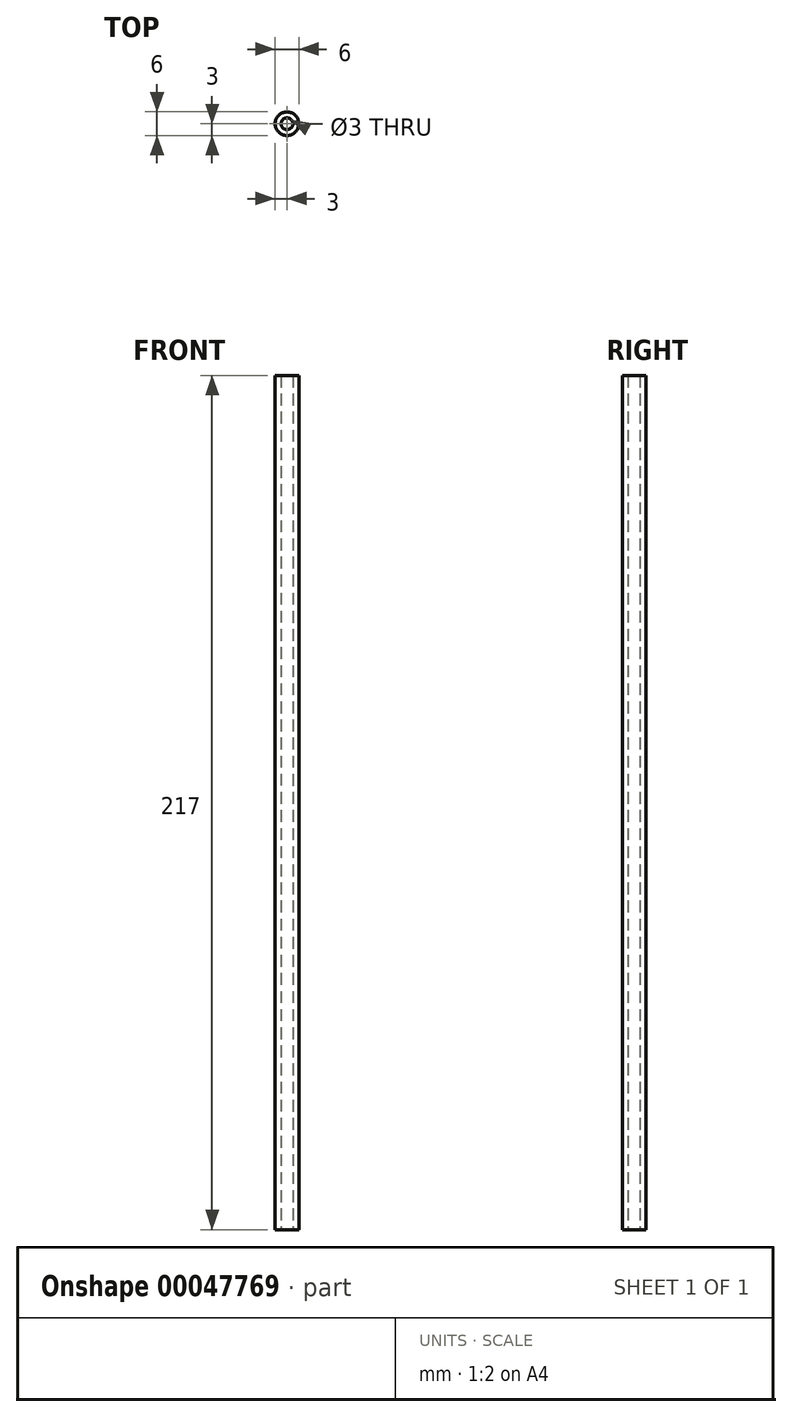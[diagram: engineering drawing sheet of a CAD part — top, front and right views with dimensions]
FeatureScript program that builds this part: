
annotation { "Feature Type Name" : "Feature", "Feature Type Description" : "" }
export const myFeature = defineFeature(function(context is Context, id is Id, definition is map)
    precondition{}
    {
        {
            var Q0;
            Q0=qCreatedBy(makeId("Top.planeOp"),FACE);
            var sketch = newSketch(context, id + "F0", { "sketchPlane" : qUnion([Q0])});
            skCircle(sketch, "E0", {"center": v(0, 0) * mm, "radius": 3 * mm});
            skCircle(sketch, "E1", {"center": v(0, 0) * mm, "radius": 1.5 * mm});
            skSolve(sketch);
        }
        {
            var Q0;
            Q0=makeQuery(id+"F0.imprint","IMPRINT",FACE,{"disambiguationData":[TD([[makeQuery(id+"F0.imprint","IMPRINT",EDGE,{"derivedFrom":sQuery(id+"F0.wireOp",EDGE,"E0")}),1.0]])]});
            extrude(context, id + "F1", {"entities" : qUnion([Q0]), "depth" : (250 - 33) * mm});
        }
    });
